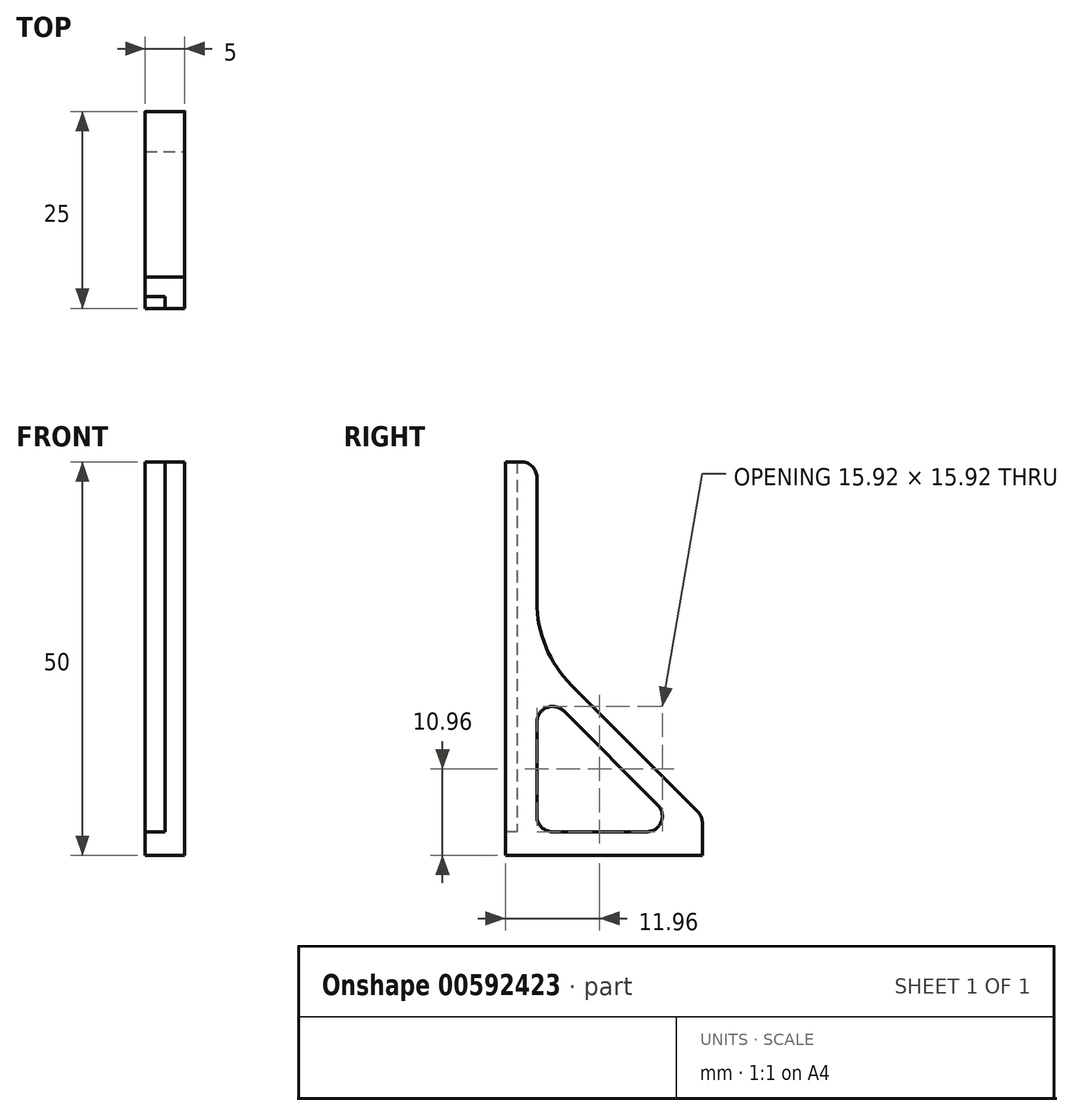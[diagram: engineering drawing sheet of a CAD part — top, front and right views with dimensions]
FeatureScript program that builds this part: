
annotation { "Feature Type Name" : "Feature", "Feature Type Description" : "" }
export const myFeature = defineFeature(function(context is Context, id is Id, definition is map)
    precondition{}
    {
        {
            var Q0;
            Q0=qCreatedBy(makeId("Right.planeOp"),FACE);
            cPlane(context, id + "F0", {"entities" : qUnion([Q0]), "cplaneType" : CPlaneType.OFFSET, "offset" : (111 / 2) * mm, "width" : 150 * mm, "height" : 150 * mm});
        }
        {
            var Q0;
            Q0=qCreatedBy(id+"F0.planeOp",FACE);
            var sketch = newSketch(context, id + "F1", { "sketchPlane" : qUnion([Q0])});
            skLineSegment(sketch, "E0.bottom", {"start": v(25, 0) * mm, "end": v(0, 0) * mm});
            skLineSegment(sketch, "E0.top", {"start": v(4, 50) * mm, "end": v(0, 50) * mm});
            skLineSegment(sketch, "E0.left", {"start": v(25, 0) * mm, "end": v(25, 5) * mm});
            skPoint(sketch, "E0.middle", {"position": v(0, 25) * mm});
            skLineSegment(sketch, "E1", {"start": v(4, 50) * mm, "end": v(4, 26) * mm});
            skPoint(sketch, "E2.newPointA", {"position": v(25, 50) * mm});
            skLineSegment(sketch, "E3", {"start": v(0, 50) * mm, "end": v(0, 0) * mm});
            skPoint(sketch, "E4.orphan", {"position": v(-25, 0) * mm});
            skLineSegment(sketch, "E5", {"start": v(4, 26) * mm, "end": v(25, 5) * mm});
            skLineSegment(sketch, "E6", {"start": v(4, 21.76) * mm, "end": v(22.76, 3) * mm});
            skLineSegment(sketch, "E7", {"start": v(22.76, 3) * mm, "end": v(4, 3) * mm});
            skLineSegment(sketch, "E8", {"start": v(4, 3) * mm, "end": v(4, 21.76) * mm});
            skSolve(sketch);
        }
        {
            var Q0;
            Q0 = qSketchRegion(id + "F1", true);
            extrude(context, id + "F2", {"entities" : qUnion([Q0]), "endBound" : BoundingType.SYMMETRIC, "depth" : 5 * mm, "offsetDistance" : 25 * mm});
        }
        {
            var Q0;
            Q0=makeQuery(id+"F2.opExtrude","SWEPT_EDGE",EDGE,{"disambiguationData":[OSD([sQuery(id+"F1.wireOp",EDGE,"E0.top"),sQuery(id+"F1.wireOp",EDGE,"E1")])]});
            var Q1;
            Q1=makeQuery(id+"F2.opExtrude","SWEPT_EDGE",EDGE,{"disambiguationData":[OSD([sQuery(id+"F1.wireOp",EDGE,"E0.left"),sQuery(id+"F1.wireOp",EDGE,"E5")])]});
            var Q2;
            Q2=makeQuery(id+"F2.opExtrude","SWEPT_EDGE",EDGE,{"disambiguationData":[OSD([sQuery(id+"F1.wireOp",EDGE,"E6"),sQuery(id+"F1.wireOp",EDGE,"E7")])]});
            var Q3;
            Q3=makeQuery(id+"F2.opExtrude","SWEPT_EDGE",EDGE,{"disambiguationData":[OSD([sQuery(id+"F1.wireOp",EDGE,"E7"),sQuery(id+"F1.wireOp",EDGE,"E8")])]});
            var Q4;
            Q4=makeQuery(id+"F2.opExtrude","SWEPT_EDGE",EDGE,{"disambiguationData":[OSD([sQuery(id+"F1.wireOp",EDGE,"E6"),sQuery(id+"F1.wireOp",EDGE,"E8")])]});
            fillet(context, id + "F3", {"entities" : qUnion([Q0, Q1, Q2, Q3, Q4]), "radius" : 2 * mm, "tangentPropagation" : true, "allowEdgeOverflow" : false});
        }
        {
            var Q0;
            Q0=makeQuery(id+"F2.opExtrude","SWEPT_EDGE",EDGE,{"disambiguationData":[OSD([sQuery(id+"F1.wireOp",EDGE,"E1"),sQuery(id+"F1.wireOp",EDGE,"E5")])]});
            fillet(context, id + "F4", {"entities" : qUnion([Q0]), "radius" : 15 * mm, "tangentPropagation" : true, "allowEdgeOverflow" : false});
        }
        {
            var Q0;
            Q0=qCreatedBy(makeId("Top.planeOp"),FACE);
            cPlane(context, id + "F5", {"entities" : qUnion([Q0]), "cplaneType" : CPlaneType.OFFSET, "offset" : 3 * mm, "width" : 150 * mm, "height" : 150 * mm});
        }
        {
            var Q0;
            Q0=qCreatedBy(id+"F5.planeOp",FACE);
            var sketch = newSketch(context, id + "F6", { "sketchPlane" : qUnion([Q0])});
            skLineSegment(sketch, "E9.bottom", {"start": v(55.5, 1.5) * mm, "end": v(53, 1.5) * mm});
            skLineSegment(sketch, "E9.top", {"start": v(55.5, -1.5) * mm, "end": v(53, -1.5) * mm});
            skLineSegment(sketch, "E9.left", {"start": v(55.5, 1.5) * mm, "end": v(55.5, -1.5) * mm});
            skLineSegment(sketch, "E9.right", {"start": v(53, 1.5) * mm, "end": v(53, -1.5) * mm});
            skPoint(sketch, "E9.middle", {"position": v(54.25, 0) * mm});
            skSolve(sketch);
        }
        {
            var Q0;
            Q0 = qSketchRegion(id + "F6", true);
            extrude(context, id + "F7", {"entities" : qUnion([Q0]), "operationType" : NewBodyOperationType.REMOVE, "endBound" : BoundingType.THROUGH_ALL, "depth" : 25 * mm, "offsetDistance" : 25 * mm});
        }
    });
